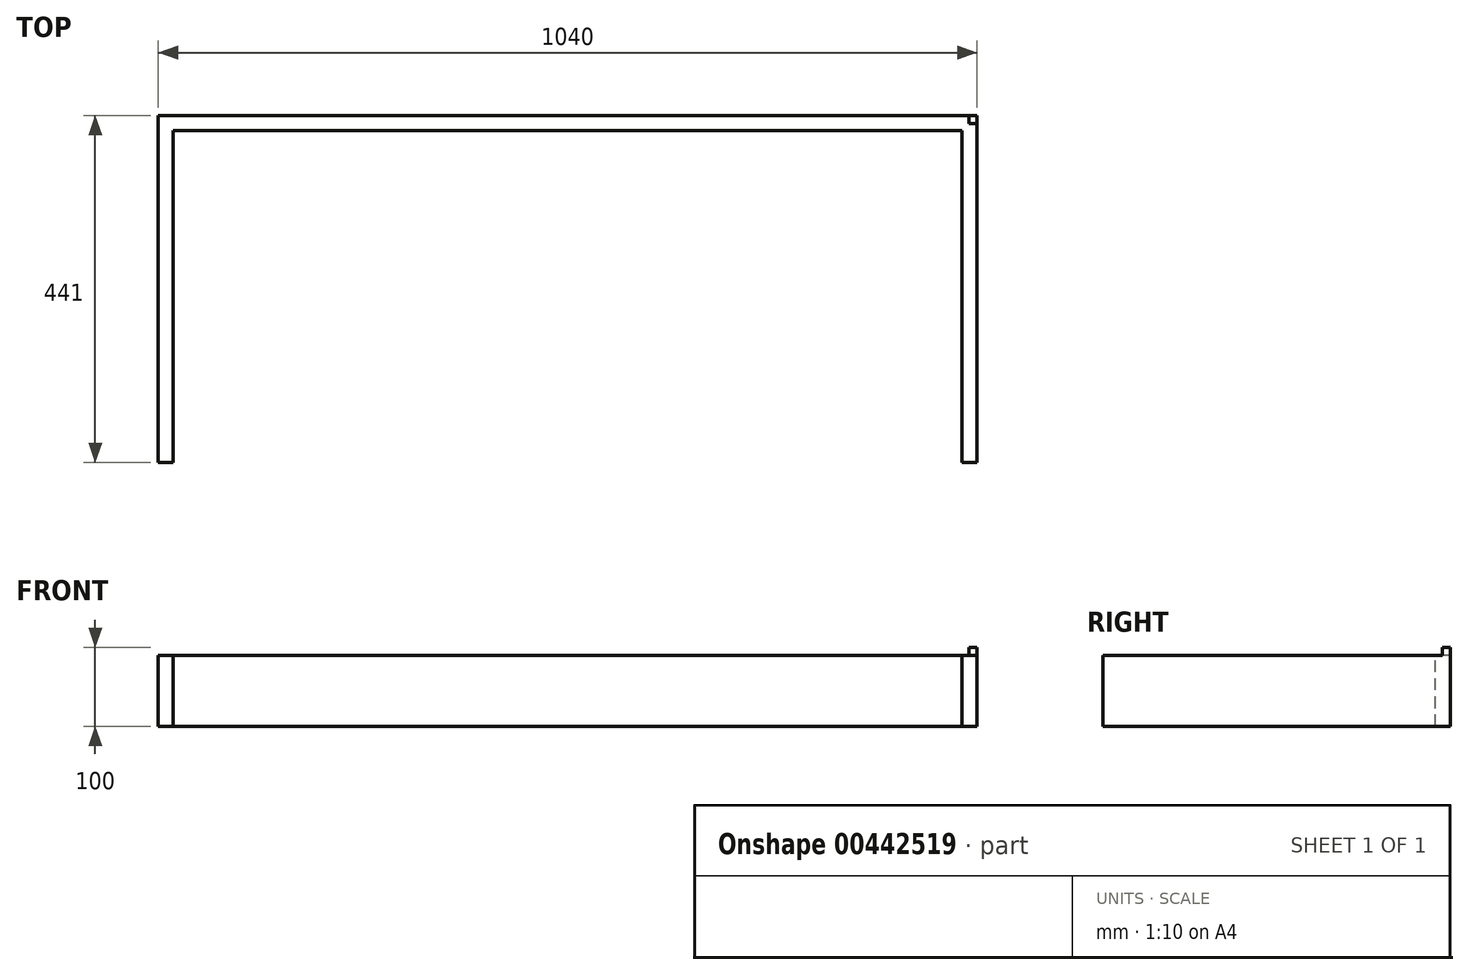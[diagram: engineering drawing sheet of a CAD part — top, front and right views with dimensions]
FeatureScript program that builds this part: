
annotation { "Feature Type Name" : "Feature", "Feature Type Description" : "" }
export const myFeature = defineFeature(function(context is Context, id is Id, definition is map)
    precondition{}
    {
        {
            var Q0;
            Q0=qCreatedBy(makeId("Top.planeOp"),FACE);
            var sketch = newSketch(context, id + "F0", { "sketchPlane" : qUnion([Q0])});
            skLineSegment(sketch, "E0", {"start": v(0, 89) * mm, "end": v(0, 530) * mm});
            skLineSegment(sketch, "E1", {"start": v(0, 530) * mm, "end": v(-1040, 530) * mm});
            skLineSegment(sketch, "E2", {"start": v(-1040, 530) * mm, "end": v(-1040, 89) * mm});
            skLineSegment(sketch, "E3", {"start": v(-1040, 530) * mm, "end": v(-1021, 530) * mm, "construction": true});
            skLineSegment(sketch, "E4", {"start": v(-1021, 530) * mm, "end": v(-1021, 511) * mm, "construction": true});
            skLineSegment(sketch, "E5", {"start": v(-1021, 89) * mm, "end": v(-1021, 511) * mm});
            skLineSegment(sketch, "E6", {"start": v(-19, 89) * mm, "end": v(-19, 511) * mm});
            skLineSegment(sketch, "E7", {"start": v(-19, 511) * mm, "end": v(-1021, 511) * mm});
            skLineSegment(sketch, "E8", {"start": v(-1040, 89) * mm, "end": v(-1021, 89) * mm});
            skLineSegment(sketch, "E9", {"start": v(0, 89) * mm, "end": v(-19, 89) * mm});
            skSolve(sketch);
        }
        {
            var Q0;
            Q0=makeQuery(id+"F0.imprint","IMPRINT",FACE,{"disambiguationData":[TD([[makeQuery(id+"F0.imprint","IMPRINT",EDGE,{"derivedFrom":sQuery(id+"F0.wireOp",EDGE,"E0")}),1.0]])]});
            extrude(context, id + "F1", {"entities" : qUnion([Q0]), "oppositeDirection" : true, "depth" : 90 * mm});
        }
        {
            var Q0;
            Q0=qCreatedBy(makeId("Top.planeOp"),FACE);
            var sketch = newSketch(context, id + "F2", { "sketchPlane" : qUnion([Q0])});
            skLineSegment(sketch, "E10", {"start": v(0, 0) * mm, "end": v(0, 530) * mm, "construction": true});
            skLineSegment(sketch, "E11.bottom", {"start": v(0, 530) * mm, "end": v(-10, 530) * mm});
            skLineSegment(sketch, "E11.top", {"start": v(0, 520) * mm, "end": v(-10, 520) * mm});
            skLineSegment(sketch, "E11.left", {"start": v(0, 530) * mm, "end": v(0, 520) * mm});
            skLineSegment(sketch, "E11.right", {"start": v(-10, 530) * mm, "end": v(-10, 520) * mm});
            skSolve(sketch);
        }
        {
            var Q0;
            Q0 = qSketchRegion(id + "F2", true);
            extrude(context, id + "F3", {"entities" : qUnion([Q0]), "operationType" : NewBodyOperationType.ADD, "depth" : 10 * mm});
        }
    });
